# Revit family: VM-5825R_Series
name_source: partatom
category: Pipe Accessories
revit_build: Autodesk Revit 2014 (Build: 20130308_1515(x64)
units: mm (PartAtom-declared; Revit-internal decimal feet)

## types (3) — shared parameters
Assembly Code = D2090800
Bolt Size = 0.625 "
CW Connection = No
CWP (PSI) = 175.00 psi
Description = Rectangular Plug Valve With Bare Stem
HW Connection = No
Manufacturer = Zoeller
Material = Metal-Zoeller-Cast Iron
Price = Prices may vary. Please consult Manufacturer Representative for most up-to-date price list.
Vent Connection = No
Waste Connection = No
Wrench = VM-3L_Series : 4L
zero-valued in all types: Default Elevation

## per-type parameters (varying)
| type | Actuator Mount Base Diameter | Actuator Mount Diameter | Actuator Mount Height | Center to Bottom | Center to Top | Flange Diameter | Flange Thickness | Height | Length | Model | No. of Bolts | Valve Size | Width |
| 6030-0084 - 2 1/2" | 2.492 " | 1.246 " | 4.62 " | 4.5 " | 9.621 " | 7 " | 0.691 " | 14.121 " | 7.5 " | VM-5825R | 4 | 2.5 " | 7.5 " |
| 6030-0085 - 3" | 2.492 " | 1.246 " | 6 " | 4.5 " | 9.621 " | 7.5 " | 0.75 " | 14.121 " | 8 " | VM-5803R | 4 | 3 " | 8 " |
| 6030-0086 - 4" | 2.992 " | 1.496 " | 6.25 " | 5.56 " | 10.94 " | 9 " | 0.75 " | 16.5 " | 9 " | VM-5804R | 8 | 4 " | 9 " |

## geometry (parser evidence)
native form markers: Sweep x4
no freeform markers — native parametric forms only
